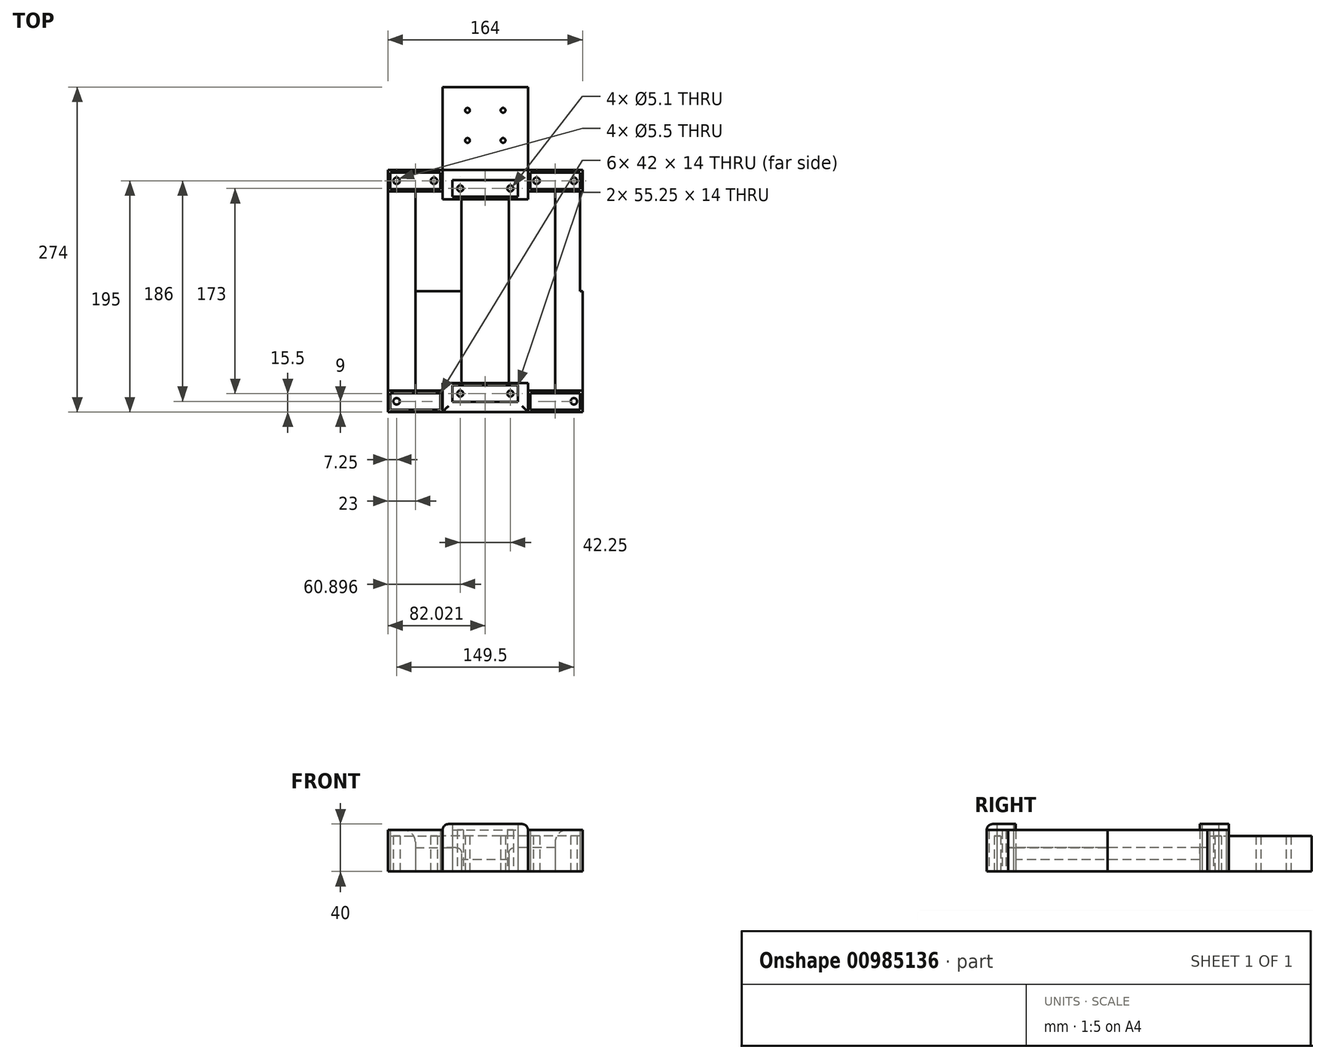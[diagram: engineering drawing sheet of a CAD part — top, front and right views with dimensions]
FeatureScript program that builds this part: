
annotation { "Feature Type Name" : "Feature", "Feature Type Description" : "" }
export const myFeature = defineFeature(function(context is Context, id is Id, definition is map)
    precondition{}
    {
        {
            var Q0;
            Q0=qCreatedBy(makeId("Top.planeOp"),FACE);
            var sketch = newSketch(context, id + "F0", { "sketchPlane" : qUnion([Q0])});
            skLineSegment(sketch, "E0.left", {"start": v(80, -100) * mm, "end": v(80, 100) * mm});
            skLineSegment(sketch, "E0.right", {"start": v(-80, -100) * mm, "end": v(-80, 100) * mm});
            skLineSegment(sketch, "E1.bottom", {"start": v(80, 100) * mm, "end": v(38, 100) * mm});
            skLineSegment(sketch, "E1.top", {"start": v(80, 86) * mm, "end": v(38, 86) * mm});
            skLineSegment(sketch, "E1.left", {"start": v(80, 100) * mm, "end": v(80, 86) * mm});
            skLineSegment(sketch, "E1.right", {"start": v(38, 100) * mm, "end": v(38, 86) * mm});
            skLineSegment(sketch, "E2.bottom", {"start": v(-80, 100) * mm, "end": v(-38, 100) * mm});
            skLineSegment(sketch, "E2.top", {"start": v(-80, 86) * mm, "end": v(-38, 86) * mm});
            skLineSegment(sketch, "E2.left", {"start": v(-80, 100) * mm, "end": v(-80, 86) * mm});
            skLineSegment(sketch, "E2.right", {"start": v(-38, 100) * mm, "end": v(-38, 86) * mm});
            skLineSegment(sketch, "E3.bottom", {"start": v(-27.6, 93.5) * mm, "end": v(27.65, 93.5) * mm});
            skLineSegment(sketch, "E3.top", {"start": v(-27.6, 79.5) * mm, "end": v(27.65, 79.5) * mm});
            skLineSegment(sketch, "E3.left", {"start": v(-27.6, 93.5) * mm, "end": v(-27.6, 79.5) * mm});
            skLineSegment(sketch, "E3.right", {"start": v(27.65, 93.5) * mm, "end": v(27.65, 79.5) * mm});
            skCircle(sketch, "E4", {"center": v(43.25, 93) * mm, "radius": 2.75 * mm});
            skPoint(sketch, "E4.centerSnap0", {"position": v(38, 93) * mm});
            skCircle(sketch, "E5", {"center": v(74.75, 93) * mm, "radius": 2.75 * mm});
            skCircle(sketch, "E6", {"center": v(-43.25, 93) * mm, "radius": 2.75 * mm});
            skPoint(sketch, "E6.centerSnap0", {"position": v(-38, 93) * mm});
            skCircle(sketch, "E7", {"center": v(-74.75, 93) * mm, "radius": 2.75 * mm});
            skPoint(sketch, "E7.centerSnap0", {"position": v(-80, 93) * mm});
            skCircle(sketch, "E8", {"center": v(-21.1, 86.5) * mm, "radius": 2.55 * mm});
            skPoint(sketch, "E8.centerSnap0", {"position": v(-27.6, 86.5) * mm});
            skCircle(sketch, "E9", {"center": v(21.15, 86.5) * mm, "radius": 2.55 * mm});
            skPoint(sketch, "E9.centerSnap0", {"position": v(27.65, 86.5) * mm});
            skLineSegment(sketch, "E10.2", {"start": v(-20, 77.5) * mm, "end": v(20, 77.5) * mm});
            skLineSegment(sketch, "E11.0", {"start": v(82, 102) * mm, "end": v(-82, 102) * mm});
            skLineSegment(sketch, "E11.1", {"start": v(82, -102) * mm, "end": v(82, 102) * mm});
            skLineSegment(sketch, "E11.3", {"start": v(-82, -102) * mm, "end": v(-82, 102) * mm});
            skLineSegment(sketch, "E12.0", {"start": v(-82, 84) * mm, "end": v(-36, 84) * mm});
            skLineSegment(sketch, "E12.1", {"start": v(-36, 102) * mm, "end": v(-36, 84) * mm});
            skLineSegment(sketch, "E13.0", {"start": v(82, 84) * mm, "end": v(36, 84) * mm});
            skLineSegment(sketch, "E13.1", {"start": v(36, 102) * mm, "end": v(36, 84) * mm});
            skLineSegment(sketch, "E14", {"start": v(-59, 84) * mm, "end": v(-59, -84) * mm});
            skLineSegment(sketch, "E15", {"start": v(59, 84) * mm, "end": v(59, -84) * mm});
            skLineSegment(sketch, "E16", {"start": v(82, 0) * mm, "end": v(80, 0) * mm});
            skLineSegment(sketch, "E17", {"start": v(80, 0) * mm, "end": v(59, 0) * mm});
            skLineSegment(sketch, "E18", {"start": v(59, 0) * mm, "end": v(0, 0) * mm});
            skLineSegment(sketch, "E19", {"start": v(0, 0) * mm, "end": v(-20, 0) * mm});
            skLineSegment(sketch, "E20", {"start": v(-59, 0) * mm, "end": v(-80, 0) * mm});
            skLineSegment(sketch, "E21.MirrorCS", {"start": v(-27.6, -93.5) * mm, "end": v(-27.6, -79.5) * mm});
            skCircle(sketch, "E22.MirrorC", {"center": v(-21.1, -86.5) * mm, "radius": 2.55 * mm});
            skCircle(sketch, "E23.MirrorC", {"center": v(74.75, -93) * mm, "radius": 2.75 * mm});
            skCircle(sketch, "E24.MirrorC", {"center": v(-74.75, -93) * mm, "radius": 2.75 * mm});
            skLineSegment(sketch, "E25.MirrorCS", {"start": v(-38, -100) * mm, "end": v(-38, -86) * mm});
            skLineSegment(sketch, "E26.MirrorCS", {"start": v(-36, -102) * mm, "end": v(-36, -84) * mm});
            skCircle(sketch, "E27.MirrorC", {"center": v(43.25, -93) * mm, "radius": 2.75 * mm});
            skCircle(sketch, "E28.MirrorC", {"center": v(21.15, -86.5) * mm, "radius": 2.55 * mm});
            skCircle(sketch, "E29.MirrorC", {"center": v(-43.25, -93) * mm, "radius": 2.75 * mm});
            skLineSegment(sketch, "E30.MirrorCS", {"start": v(27.65, -93.5) * mm, "end": v(27.65, -79.5) * mm});
            skLineSegment(sketch, "E31.MirrorCS", {"start": v(38, -100) * mm, "end": v(38, -86) * mm});
            skPoint(sketch, "E32.MirrorP", {"position": v(-38, -93) * mm});
            skLineSegment(sketch, "E33.MirrorCS", {"start": v(36, -102) * mm, "end": v(36, -84) * mm});
            skLineSegment(sketch, "E34.MirrorCS", {"start": v(80, -100) * mm, "end": v(80, -86) * mm});
            skPoint(sketch, "E35.MirrorP", {"position": v(-27.6, -86.5) * mm});
            skLineSegment(sketch, "E36.MirrorCS", {"start": v(-80, -100) * mm, "end": v(-80, -86) * mm});
            skLineSegment(sketch, "E37.MirrorCS", {"start": v(-82, -84) * mm, "end": v(-36, -84) * mm});
            skLineSegment(sketch, "E38.MirrorCS", {"start": v(-80, -86) * mm, "end": v(-38, -86) * mm});
            skPoint(sketch, "E39.MirrorP", {"position": v(38, -93) * mm});
            skLineSegment(sketch, "E40.MirrorCS", {"start": v(80, -86) * mm, "end": v(38, -86) * mm});
            skLineSegment(sketch, "E41.MirrorCS", {"start": v(-27.6, -79.5) * mm, "end": v(27.65, -79.5) * mm});
            skLineSegment(sketch, "E42.MirrorCS", {"start": v(82, -102) * mm, "end": v(-82, -102) * mm});
            skLineSegment(sketch, "E43.MirrorCS", {"start": v(82, -84) * mm, "end": v(36, -84) * mm});
            skPoint(sketch, "E44.MirrorP", {"position": v(27.65, -86.5) * mm});
            skLineSegment(sketch, "E45.MirrorCS", {"start": v(-27.6, -93.5) * mm, "end": v(27.65, -93.5) * mm});
            skLineSegment(sketch, "E46.MirrorCS", {"start": v(80, -100) * mm, "end": v(38, -100) * mm});
            skPoint(sketch, "E47.MirrorP", {"position": v(-80, -93) * mm});
            skLineSegment(sketch, "E48.MirrorCS", {"start": v(-80, -100) * mm, "end": v(-38, -100) * mm});
            skPoint(sketch, "E49", {"position": v(-80, 0) * mm});
            skPoint(sketch, "E50", {"position": v(-82, 0) * mm});
            skPoint(sketch, "E51", {"position": v(-80, 84) * mm});
            skPoint(sketch, "E52", {"position": v(-82, 84) * mm});
            skPoint(sketch, "E53", {"position": v(80, 84) * mm});
            skPoint(sketch, "E54", {"position": v(82, 84) * mm});
            skPoint(sketch, "E55", {"position": v(80, 0) * mm});
            skPoint(sketch, "E56", {"position": v(82, 0) * mm});
            skLineSegment(sketch, "E57", {"start": v(-82, 84) * mm, "end": v(-80, 84) * mm});
            skLineSegment(sketch, "E58", {"start": v(80, 84) * mm, "end": v(82, 84) * mm});
            skLineSegment(sketch, "E59", {"start": v(36, 102) * mm, "end": v(36, 100) * mm});
            skLineSegment(sketch, "E60", {"start": v(-82, 0) * mm, "end": v(-80, 0) * mm});
            skLineSegment(sketch, "E61", {"start": v(-82, -84) * mm, "end": v(-80, -84) * mm});
            skLineSegment(sketch, "E62", {"start": v(80, -84) * mm, "end": v(82, -84) * mm});
            skLineSegment(sketch, "E63", {"start": v(80, 0) * mm, "end": v(82, 0) * mm});
            skLineSegment(sketch, "E64", {"start": v(-38, 100) * mm, "end": v(-80, 100) * mm});
            skLineSegment(sketch, "E65", {"start": v(-59, -84) * mm, "end": v(-59, 0) * mm});
            skLineSegment(sketch, "E66", {"start": v(-59, 0) * mm, "end": v(-20, 0) * mm});
            skLineSegment(sketch, "E67", {"start": v(36, -102) * mm, "end": v(36, -77.5) * mm});
            skLineSegment(sketch, "E68", {"start": v(-36, -102) * mm, "end": v(-36, -77.5) * mm});
            skLineSegment(sketch, "E69", {"start": v(36, -77.5) * mm, "end": v(-36, -77.5) * mm});
            skLineSegment(sketch, "E70", {"start": v(20, -77.5) * mm, "end": v(20, 77.5) * mm});
            skLineSegment(sketch, "E71", {"start": v(-20, 77.5) * mm, "end": v(-20, -77.5) * mm});
            skLineSegment(sketch, "E72", {"start": v(36, 84) * mm, "end": v(36, 77.5) * mm});
            skLineSegment(sketch, "E73", {"start": v(36, 77.5) * mm, "end": v(20, 77.5) * mm});
            skLineSegment(sketch, "E74", {"start": v(-36, 84) * mm, "end": v(-36, 77.5) * mm});
            skLineSegment(sketch, "E75", {"start": v(-20, 77.5) * mm, "end": v(-36, 77.5) * mm});
            skLineSegment(sketch, "E76.bottom", {"start": v(-36, 102) * mm, "end": v(36, 102) * mm});
            skLineSegment(sketch, "E76.top", {"start": v(-36, 172) * mm, "end": v(36, 172) * mm});
            skLineSegment(sketch, "E76.left", {"start": v(-36, 102) * mm, "end": v(-36, 172) * mm});
            skLineSegment(sketch, "E76.right", {"start": v(36, 102) * mm, "end": v(36, 172) * mm});
            skLineSegment(sketch, "E77", {"start": v(0, 102) * mm, "end": v(0, 172) * mm});
            skCircle(sketch, "E78", {"center": v(-15, 127) * mm, "radius": 2 * mm});
            skCircle(sketch, "E79", {"center": v(-15, 152.4) * mm, "radius": 2 * mm});
            skCircle(sketch, "E80.MirrorC", {"center": v(15, 127) * mm, "radius": 2 * mm});
            skCircle(sketch, "E81.MirrorC", {"center": v(15, 152.4) * mm, "radius": 2 * mm});
            skSolve(sketch);
        }
        {
            var Q0;
            Q0=makeQuery(id+"F0.imprint","IMPRINT",FACE,{"disambiguationData":[TD([[makeQuery(id+"F0.imprint","IMPRINT",EDGE,{"derivedFrom":sQuery(id+"F0.wireOp",EDGE,"E2.bottom")}),-1.0]])]});
            var Q1;
            Q1=makeQuery(id+"F0.imprint","IMPRINT",FACE,{"disambiguationData":[TD([[makeQuery(id+"F0.imprint","IMPRINT",EDGE,{"derivedFrom":sQuery(id+"F0.wireOp",EDGE,"E1.bottom")}),1.0]])]});
            var Q2;
            Q2=makeQuery(id+"F0.imprint","IMPRINT",FACE,{"disambiguationData":[TD([[makeQuery(id+"F0.imprint","IMPRINT",EDGE,{"derivedFrom":sQuery(id+"F0.wireOp",EDGE,"ixyLcDFA-bc6J-Iatk-8igf-DqBppD76QXGP.bottom")}),1.0]])]});
            var Q3;
            Q3=makeQuery(id+"F0.imprint","IMPRINT",FACE,{"disambiguationData":[TD([[makeQuery(id+"F0.imprint","IMPRINT",EDGE,{"derivedFrom":sQuery(id+"F0.wireOp",EDGE,"OfFNVEAe-m7io-4Cfx-FPli-c9zqfDngx50L.bottom")}),-1.0]])]});
            var Q4;
            Q4=makeQuery(id+"F0.imprint","IMPRINT",FACE,{"disambiguationData":[TD([[makeQuery(id+"F0.imprint","IMPRINT",EDGE,{"derivedFrom":sQuery(id+"F0.wireOp",EDGE,"E24.MirrorC")}),1.0]])]});
            var Q5;
            Q5=makeQuery(id+"F0.imprint","IMPRINT",FACE,{"disambiguationData":[TD([[makeQuery(id+"F0.imprint","IMPRINT",EDGE,{"derivedFrom":sQuery(id+"F0.wireOp",EDGE,"E23.MirrorC")}),1.0]])]});
            var Q6;
            Q6=makeQuery(id+"F0.imprint","IMPRINT",FACE,{"disambiguationData":[TD([[makeQuery(id+"F0.imprint","IMPRINT",EDGE,{"derivedFrom":sQuery(id+"F0.wireOp",EDGE,"E1.top")}),-1.0]])]});
            var Q7;
            Q7=makeQuery(id+"F0.imprint","IMPRINT",FACE,{"disambiguationData":[TD([[makeQuery(id+"F0.imprint","IMPRINT",EDGE,{"derivedFrom":sQuery(id+"F0.wireOp",EDGE,"E2.top")}),1.0]])]});
            var Q8;
            Q8=makeQuery(id+"F0.imprint","IMPRINT",FACE,{"disambiguationData":[TD([[makeQuery(id+"F0.imprint","IMPRINT",EDGE,{"derivedFrom":sQuery(id+"F0.wireOp",EDGE,"E7")}),-1.0]])]});
            var Q9;
            Q9=makeQuery(id+"F0.imprint","IMPRINT",FACE,{"disambiguationData":[TD([[makeQuery(id+"F0.imprint","IMPRINT",EDGE,{"derivedFrom":sQuery(id+"F0.wireOp",EDGE,"E1.right")}),1.0]])]});
            extrude(context, id + "F1", {"entities" : qUnion([Q0, Q1, Q2, Q3, Q4, Q5, Q6, Q7, Q8, Q9]), "depth" : 30 * mm, "offsetDistance" : 25 * mm});
        }
        {
            var Q0;
            {var subQ1=sQuery(id+"F0.wireOp",EDGE,"E1.bottom");Q0=makeQuery(id+"F0.imprint","IMPRINT",FACE,{"disambiguationData":[TD([[makeQuery(id+"F0.imprint","IMPRINT",EDGE,{"derivedFrom":subQ1}),-1.0]])]});}
            var Q1;
            {var subQ0=sQuery(id+"F0.wireOp",EDGE,"E1.top");Q1=makeQuery(id+"F0.imprint","IMPRINT",FACE,{"disambiguationData":[TD([[makeQuery(id+"F0.imprint","IMPRINT",EDGE,{"derivedFrom":subQ0}),1.0]])]});}
            var Q2;
            {var subQ0=sQuery(id+"F0.wireOp",EDGE,"E2.bottom");Q2=makeQuery(id+"F0.imprint","IMPRINT",FACE,{"disambiguationData":[TD([[makeQuery(id+"F0.imprint","IMPRINT",EDGE,{"derivedFrom":subQ0}),1.0]])]});}
            var Q3;
            {var subQ4=sQuery(id+"F0.wireOp",EDGE,"E2.top");Q3=makeQuery(id+"F0.imprint","IMPRINT",FACE,{"disambiguationData":[TD([[makeQuery(id+"F0.imprint","IMPRINT",EDGE,{"derivedFrom":subQ4}),-1.0]])]});}
            var Q4;
            {var subQ1=sQuery(id+"F0.wireOp",EDGE,"ixyLcDFA-bc6J-Iatk-8igf-DqBppD76QXGP.top");Q4=makeQuery(id+"F0.imprint","IMPRINT",FACE,{"disambiguationData":[TD([[makeQuery(id+"F0.imprint","IMPRINT",EDGE,{"derivedFrom":subQ1}),1.0]])]});}
            var Q5;
            {var subQ4=sQuery(id+"F0.wireOp",EDGE,"ixyLcDFA-bc6J-Iatk-8igf-DqBppD76QXGP.bottom");Q5=makeQuery(id+"F0.imprint","IMPRINT",FACE,{"disambiguationData":[TD([[makeQuery(id+"F0.imprint","IMPRINT",EDGE,{"derivedFrom":subQ4}),-1.0]])]});}
            var Q6;
            {var subQ4=sQuery(id+"F0.wireOp",EDGE,"OfFNVEAe-m7io-4Cfx-FPli-c9zqfDngx50L.top");Q6=makeQuery(id+"F0.imprint","IMPRINT",FACE,{"disambiguationData":[TD([[makeQuery(id+"F0.imprint","IMPRINT",EDGE,{"derivedFrom":subQ4}),-1.0]])]});}
            var Q7;
            {var subQ1=sQuery(id+"F0.wireOp",EDGE,"OfFNVEAe-m7io-4Cfx-FPli-c9zqfDngx50L.bottom");Q7=makeQuery(id+"F0.imprint","IMPRINT",FACE,{"disambiguationData":[TD([[makeQuery(id+"F0.imprint","IMPRINT",EDGE,{"derivedFrom":subQ1}),1.0]])]});}
            var Q8;
            {var subQ9=sQuery(id+"F0.wireOp",EDGE,"E25.MirrorCS");Q8=makeQuery(id+"F0.imprint","IMPRINT",FACE,{"disambiguationData":[TD([[makeQuery(id+"F0.imprint","IMPRINT",EDGE,{"derivedFrom":subQ9}),-1.0]])]});}
            var Q9;
            {var subQ0=sQuery(id+"F0.wireOp",EDGE,"E36.MirrorCS");Q9=makeQuery(id+"F0.imprint","IMPRINT",FACE,{"disambiguationData":[TD([[makeQuery(id+"F0.imprint","IMPRINT",EDGE,{"derivedFrom":subQ0}),1.0]])]});}
            var Q10;
            {var subQ8=sQuery(id+"F0.wireOp",EDGE,"E31.MirrorCS");Q10=makeQuery(id+"F0.imprint","IMPRINT",FACE,{"disambiguationData":[TD([[makeQuery(id+"F0.imprint","IMPRINT",EDGE,{"derivedFrom":subQ8}),1.0]])]});}
            var Q11;
            {var subQ0=sQuery(id+"F0.wireOp",EDGE,"E34.MirrorCS");Q11=makeQuery(id+"F0.imprint","IMPRINT",FACE,{"disambiguationData":[TD([[makeQuery(id+"F0.imprint","IMPRINT",EDGE,{"derivedFrom":subQ0}),-1.0]])]});}
            var Q12;
            {var subQ0=sQuery(id+"F0.wireOp",EDGE,"E12.1");Q12=makeQuery(id+"F0.imprint","IMPRINT",FACE,{"disambiguationData":[TD([[makeQuery(id+"F0.imprint","IMPRINT",EDGE,{"derivedFrom":subQ0}),-1.0]])]});}
            var Q13;
            Q13=makeQuery(id+"F0.imprint","IMPRINT",FACE,{"disambiguationData":[TD([[makeQuery(id+"F0.imprint","IMPRINT",EDGE,{"derivedFrom":sQuery(id+"F0.wireOp",EDGE,"E1.right")}),-1.0]])]});
            extrude(context, id + "F2", {"entities" : qUnion([Q0, Q1, Q2, Q3, Q4, Q5, Q6, Q7, Q8, Q9, Q10, Q11, Q12, Q13]), "depth" : 35 * mm, "offsetDistance" : 25 * mm});
        }
        {
            var Q0;
            Q0=makeQuery(id+"F0.imprint","IMPRINT",FACE,{"disambiguationData":[TD([[makeQuery(id+"F0.imprint","IMPRINT",EDGE,{"derivedFrom":sQuery(id+"F0.wireOp",EDGE,"E3.bottom")}),-1.0]])]});
            var Q1;
            Q1=makeQuery(id+"F0.imprint","IMPRINT",FACE,{"disambiguationData":[TD([[makeQuery(id+"F0.imprint","IMPRINT",EDGE,{"derivedFrom":sQuery(id+"F0.wireOp",EDGE,"UbgPOWGu-DJYq-DXMP-9FCt-mUyMvT1JZ0WB.bottom")}),1.0]])]});
            var Q2;
            Q2=makeQuery(id+"F0.imprint","IMPRINT",FACE,{"disambiguationData":[TD([[makeQuery(id+"F0.imprint","IMPRINT",EDGE,{"derivedFrom":sQuery(id+"F0.wireOp",EDGE,"E21.MirrorCS")}),-1.0]])]});
            var Q3;
            Q3=makeQuery(id+"F0.imprint","IMPRINT",FACE,{"disambiguationData":[TD([[makeQuery(id+"F0.imprint","IMPRINT",EDGE,{"derivedFrom":sQuery(id+"F0.wireOp",EDGE,"E8")}),-1.0]])]});
            extrude(context, id + "F3", {"entities" : qUnion([Q0, Q1, Q2, Q3]), "depth" : 35 * mm, "offsetDistance" : 25 * mm});
        }
        {
            var Q0;
            Q0=makeQuery(id+"F0.imprint","IMPRINT",FACE,{"disambiguationData":[TD([[makeQuery(id+"F0.imprint","IMPRINT",EDGE,{"derivedFrom":sQuery(id+"F0.wireOp",EDGE,"UbgPOWGu-DJYq-DXMP-9FCt-mUyMvT1JZ0WB.top")}),1.0]])]});
            var Q1;
            {var subQ0=sQuery(id+"F0.wireOp",EDGE,"UbgPOWGu-DJYq-DXMP-9FCt-mUyMvT1JZ0WB.bottom");Q1=makeQuery(id+"F0.imprint","IMPRINT",FACE,{"disambiguationData":[TD([[makeQuery(id+"F0.imprint","IMPRINT",EDGE,{"derivedFrom":subQ0}),-1.0]])]});}
            var Q2;
            Q2=makeQuery(id+"F0.imprint","IMPRINT",FACE,{"disambiguationData":[TD([[makeQuery(id+"F0.imprint","IMPRINT",EDGE,{"derivedFrom":sQuery(id+"F0.wireOp",EDGE,"E3.bottom")}),1.0]])]});
            var Q3;
            Q3=makeQuery(id+"F0.imprint","IMPRINT",FACE,{"disambiguationData":[TD([[makeQuery(id+"F0.imprint","IMPRINT",EDGE,{"derivedFrom":sQuery(id+"F0.wireOp",EDGE,"E21.MirrorCS")}),1.0]])]});
            var Q4;
            {var subQ10=sQuery(id+"F0.wireOp",EDGE,"qVaEij7k-nwjH-SPuv-bkV3-loI1qYVZHqOl");Q4=makeQuery(id+"F0.imprint","IMPRINT",FACE,{"disambiguationData":[TD([[makeQuery(id+"F0.imprint","IMPRINT",EDGE,{"derivedFrom":subQ10}),1.0]])]});}
            var Q5;
            {var subQ2=sQuery(id+"F0.wireOp",EDGE,"E12.1");Q5=makeQuery(id+"F0.imprint","IMPRINT",FACE,{"disambiguationData":[TD([[makeQuery(id+"F0.imprint","IMPRINT",EDGE,{"derivedFrom":subQ2}),1.0]])]});}
            extrude(context, id + "F4", {"entities" : qUnion([Q0, Q1, Q2, Q3, Q4, Q5]), "depth" : 40 * mm, "offsetDistance" : 25 * mm});
        }
        {
            var Q0;
            {var subQ0=sQuery(id+"F0.wireOp",EDGE,"B5Z4tnl7-zgow-OxXi-EMlq-tNImqLLrCm8m");Q0=makeQuery(id+"F0.imprint","IMPRINT",FACE,{"disambiguationData":[TD([[makeQuery(id+"F0.imprint","IMPRINT",EDGE,{"derivedFrom":subQ0}),-1.0]])]});}
            var Q1;
            {var subQ0=sQuery(id+"F0.wireOp",EDGE,"QeB9K7Id-tPgK-ENxB-AcUf-C9a2ECh6eyOd");Q1=makeQuery(id+"F0.imprint","IMPRINT",FACE,{"disambiguationData":[TD([[makeQuery(id+"F0.imprint","IMPRINT",EDGE,{"derivedFrom":subQ0}),1.0]])]});}
            var Q2;
            {var subQ3=sQuery(id+"F0.wireOp",EDGE,"b8552f40-8e1e-479f-b918-41427cde39ce1.MirrorCS");Q2=makeQuery(id+"F0.imprint","IMPRINT",FACE,{"disambiguationData":[TD([[makeQuery(id+"F0.imprint","IMPRINT",EDGE,{"derivedFrom":subQ3}),1.0]])]});}
            var Q3;
            {var subQ0=sQuery(id+"F0.wireOp",EDGE,"b8552f40-8e1e-479f-b918-41427cde39ce12.MirrorCS");var subQ1=sQuery(id+"F0.wireOp",EDGE,"tyTy7cMs-IovG-FTIG-svWU-RZ1L8kjrpybv");var subQ2=makeQuery(id+"F0.imprint","INTERSECT",VERTEX,{"derivedFrom":[subQ1,subQ0]});Q3=makeQuery(id+"F0.imprint","IMPRINT",FACE,{"disambiguationData":[TD([[makeQuery(id+"F0.imprint","IMPRINT",EDGE,{"disambiguationData":[TD([[subQ2,1.0]])],"derivedFrom":subQ1}),1.0]])]});}
            var Q4;
            {var subQ5=sQuery(id+"F0.wireOp",EDGE,"OglT18Nm-HUVC-Pnps-TW8b-jYMKbPkvL7uU");Q4=makeQuery(id+"F0.imprint","IMPRINT",FACE,{"disambiguationData":[TD([[makeQuery(id+"F0.imprint","IMPRINT",EDGE,{"derivedFrom":subQ5}),-1.0]])]});}
            var Q5;
            {var subQ3=sQuery(id+"F0.wireOp",EDGE,"C9wmSgbj-CDq8-hHrZ-SwvS-kieF0k5TPAWY");Q5=makeQuery(id+"F0.imprint","IMPRINT",FACE,{"disambiguationData":[TD([[makeQuery(id+"F0.imprint","IMPRINT",EDGE,{"derivedFrom":subQ3}),1.0]])]});}
            var Q6;
            {var subQ1=sQuery(id+"F0.wireOp",EDGE,"E14");Q6=makeQuery(id+"F0.imprint","IMPRINT",FACE,{"disambiguationData":[TD([[makeQuery(id+"F0.imprint","IMPRINT",EDGE,{"derivedFrom":subQ1}),1.0]])]});}
            var Q7;
            {var subQ6=sQuery(id+"F0.wireOp",EDGE,"E65");Q7=makeQuery(id+"F0.imprint","IMPRINT",FACE,{"disambiguationData":[TD([[makeQuery(id+"F0.imprint","IMPRINT",EDGE,{"derivedFrom":subQ6}),-1.0]])]});}
            var Q8;
            {var subQ0=sQuery(id+"F0.wireOp",EDGE,"E43.MirrorCS");var subQ1=sQuery(id+"F0.wireOp",EDGE,"E15");var subQ2=makeQuery(id+"F0.imprint","INTERSECT",VERTEX,{"derivedFrom":[subQ1,subQ0]});Q8=makeQuery(id+"F0.imprint","IMPRINT",FACE,{"disambiguationData":[TD([[makeQuery(id+"F0.imprint","IMPRINT",EDGE,{"disambiguationData":[TD([[subQ2,-1.0]])],"derivedFrom":subQ0}),-1.0]])]});}
            var Q9;
            {var subQ3=sQuery(id+"F0.wireOp",EDGE,"E72");Q9=makeQuery(id+"F0.imprint","IMPRINT",FACE,{"disambiguationData":[TD([[makeQuery(id+"F0.imprint","IMPRINT",EDGE,{"derivedFrom":subQ3}),1.0]])]});}
            extrude(context, id + "F5", {"entities" : qUnion([Q0, Q1, Q2, Q3, Q4, Q5, Q6, Q7, Q8, Q9]), "depth" : 20 * mm, "offsetDistance" : 25 * mm});
        }
        {
            var Q0;
            Q0=makeQuery(id+"F0.imprint","IMPRINT",FACE,{"disambiguationData":[TD([[makeQuery(id+"F0.imprint","IMPRINT",EDGE,{"derivedFrom":sQuery(id+"F0.wireOp",EDGE,"E10.2")}),-1.0]])]});
            var Q1;
            {var subQ0=sQuery(id+"F0.wireOp",EDGE,"E19");Q1=makeQuery(id+"F0.imprint","IMPRINT",FACE,{"disambiguationData":[TD([[makeQuery(id+"F0.imprint","IMPRINT",EDGE,{"derivedFrom":subQ0}),1.0]])]});}
            var Q2;
            Q2=makeQuery(id+"F0.imprint","IMPRINT",FACE,{"disambiguationData":[TD([[makeQuery(id+"F0.imprint","IMPRINT",EDGE,{"derivedFrom":sQuery(id+"F0.wireOp",EDGE,"P8kr6sO9-KCci-oqqV-lbCG-12AdMWymWlzo")}),-1.0]])]});
            var Q3;
            {var subQ1=sQuery(id+"F0.wireOp",EDGE,"E19");Q3=makeQuery(id+"F0.imprint","IMPRINT",FACE,{"disambiguationData":[TD([[makeQuery(id+"F0.imprint","IMPRINT",EDGE,{"derivedFrom":subQ1}),-1.0]])]});}
            extrude(context, id + "F6", {"entities" : qUnion([Q0, Q1, Q2, Q3]), "depth" : 10 * mm, "offsetDistance" : 25 * mm});
        }
        {
            var Q0;
            {var subQ1=sQuery(id+"F0.wireOp",EDGE,"E2.bottom");Q0=makeQuery(id+"F0.imprint","IMPRINT",FACE,{"disambiguationData":[TD([[makeQuery(id+"F0.imprint","IMPRINT",EDGE,{"derivedFrom":subQ1}),1.0]])]});}
            var Q1;
            {var subQ0=sQuery(id+"F0.wireOp",EDGE,"E1.bottom");Q1=makeQuery(id+"F0.imprint","IMPRINT",FACE,{"disambiguationData":[TD([[makeQuery(id+"F0.imprint","IMPRINT",EDGE,{"derivedFrom":subQ0}),-1.0]])]});}
            var Q2;
            {var subQ0=sQuery(id+"F0.wireOp",EDGE,"b3zk2VQc-cE7L-r2go-jK9M-t36oJfSmH84w");var subQ1=sQuery(id+"F0.wireOp",EDGE,"E0.left");var subQ2=makeQuery(id+"F0.imprint","INTERSECT",VERTEX,{"derivedFrom":[subQ1,subQ0]});Q2=makeQuery(id+"F0.imprint","IMPRINT",FACE,{"disambiguationData":[TD([[makeQuery(id+"F0.imprint","IMPRINT",EDGE,{"disambiguationData":[TD([[subQ2,-1.0]])],"derivedFrom":subQ1}),-1.0]])]});}
            var Q3;
            {var subQ0=sQuery(id+"F0.wireOp",EDGE,"E36.MirrorCS");Q3=makeQuery(id+"F0.imprint","IMPRINT",FACE,{"disambiguationData":[TD([[makeQuery(id+"F0.imprint","IMPRINT",EDGE,{"derivedFrom":subQ0}),1.0]])]});}
            var Q4;
            {var subQ0=sQuery(id+"F0.wireOp",EDGE,"E16");Q4=makeQuery(id+"F0.imprint","IMPRINT",FACE,{"disambiguationData":[TD([[makeQuery(id+"F0.imprint","IMPRINT",EDGE,{"derivedFrom":subQ0}),1.0]])]});}
            var Q5;
            {var subQ0=sQuery(id+"F0.wireOp",EDGE,"E34.MirrorCS");Q5=makeQuery(id+"F0.imprint","IMPRINT",FACE,{"disambiguationData":[TD([[makeQuery(id+"F0.imprint","IMPRINT",EDGE,{"derivedFrom":subQ0}),-1.0]])]});}
            var Q6;
            {var subQ0=sQuery(id+"F0.wireOp",EDGE,"E17");Q6=makeQuery(id+"F0.imprint","IMPRINT",FACE,{"disambiguationData":[TD([[makeQuery(id+"F0.imprint","IMPRINT",EDGE,{"derivedFrom":subQ0}),1.0]])]});}
            var Q7;
            {var subQ0=sQuery(id+"F0.wireOp",EDGE,"E37.MirrorCS");var subQ1=sQuery(id+"F0.wireOp",EDGE,"E0.right");var subQ2=makeQuery(id+"F0.imprint","INTERSECT",VERTEX,{"derivedFrom":[subQ1,subQ0]});Q7=makeQuery(id+"F0.imprint","IMPRINT",FACE,{"disambiguationData":[TD([[makeQuery(id+"F0.imprint","IMPRINT",EDGE,{"disambiguationData":[TD([[subQ2,-1.0]])],"derivedFrom":subQ1}),-1.0]])]});}
            var Q8;
            {var subQ0=sQuery(id+"F0.wireOp",EDGE,"b3zk2VQc-cE7L-r2go-jK9M-t36oJfSmH84w");var subQ1=sQuery(id+"F0.wireOp",EDGE,"E0.left");var subQ2=makeQuery(id+"F0.imprint","INTERSECT",VERTEX,{"derivedFrom":[subQ1,subQ0]});Q8=makeQuery(id+"F0.imprint","IMPRINT",FACE,{"disambiguationData":[TD([[makeQuery(id+"F0.imprint","IMPRINT",EDGE,{"disambiguationData":[TD([[subQ2,-1.0]])],"derivedFrom":subQ1}),1.0]])]});}
            var Q9;
            {var subQ0=sQuery(id+"F0.wireOp",EDGE,"E20");Q9=makeQuery(id+"F0.imprint","IMPRINT",FACE,{"disambiguationData":[TD([[makeQuery(id+"F0.imprint","IMPRINT",EDGE,{"derivedFrom":subQ0}),-1.0]])]});}
            var Q10;
            {var subQ3=sQuery(id+"F0.wireOp",EDGE,"E57");Q10=makeQuery(id+"F0.imprint","IMPRINT",FACE,{"disambiguationData":[TD([[makeQuery(id+"F0.imprint","IMPRINT",EDGE,{"derivedFrom":subQ3}),-1.0]])]});}
            var Q11;
            {var subQ0=sQuery(id+"F0.wireOp",EDGE,"E37.MirrorCS");var subQ1=sQuery(id+"F0.wireOp",EDGE,"E0.right");var subQ2=makeQuery(id+"F0.imprint","INTERSECT",VERTEX,{"derivedFrom":[subQ1,subQ0]});Q11=makeQuery(id+"F0.imprint","IMPRINT",FACE,{"disambiguationData":[TD([[makeQuery(id+"F0.imprint","IMPRINT",EDGE,{"disambiguationData":[TD([[subQ2,-1.0]])],"derivedFrom":subQ1}),1.0]])]});}
            var Q12;
            {var subQ0=sQuery(id+"F0.wireOp",EDGE,"E57");Q12=makeQuery(id+"F0.imprint","IMPRINT",FACE,{"disambiguationData":[TD([[makeQuery(id+"F0.imprint","IMPRINT",EDGE,{"derivedFrom":subQ0}),-1.0]])]});}
            var Q13;
            {var subQ2=sQuery(id+"F0.wireOp",EDGE,"E62");Q13=makeQuery(id+"F0.imprint","IMPRINT",FACE,{"disambiguationData":[TD([[makeQuery(id+"F0.imprint","IMPRINT",EDGE,{"derivedFrom":subQ2}),1.0]])]});}
            var Q14;
            {var subQ0=sQuery(id+"F0.wireOp",EDGE,"E17");Q14=makeQuery(id+"F0.imprint","IMPRINT",FACE,{"disambiguationData":[TD([[makeQuery(id+"F0.imprint","IMPRINT",EDGE,{"derivedFrom":subQ0}),-1.0]])]});}
            var Q15;
            {var subQ0=sQuery(id+"F0.wireOp",EDGE,"E63");Q15=makeQuery(id+"F0.imprint","IMPRINT",FACE,{"disambiguationData":[TD([[makeQuery(id+"F0.imprint","IMPRINT",EDGE,{"derivedFrom":subQ0}),1.0]])]});}
            var Q16;
            {var subQ0=sQuery(id+"F0.wireOp",EDGE,"E60");Q16=makeQuery(id+"F0.imprint","IMPRINT",FACE,{"disambiguationData":[TD([[makeQuery(id+"F0.imprint","IMPRINT",EDGE,{"derivedFrom":subQ0}),1.0]])]});}
            extrude(context, id + "F7", {"entities" : qUnion([Q0, Q1, Q2, Q3, Q4, Q5, Q6, Q7, Q8, Q9, Q10, Q11, Q12, Q13, Q14, Q15, Q16]), "depth" : 35 * mm, "offsetDistance" : 25 * mm});
        }
        {
            var Q0;
            Q0=makeQuery(id+"F7.opExtrude","CAP_EDGE",EDGE,{"disambiguationData":[OSD([sQuery(id+"F0.wireOp",EDGE,"E15")])],"isStart":false});
            var Q1;
            Q1=makeQuery(id+"F7.opExtrude","CAP_EDGE",EDGE,{"disambiguationData":[OSD([sQuery(id+"F0.wireOp",EDGE,"E14"),sQuery(id+"F0.wireOp",EDGE,"E65")])],"isStart":false});
            fillet(context, id + "F8", {"entities" : qUnion([Q0, Q1]), "radius" : 10 * mm, "tangentPropagation" : true, "allowEdgeOverflow" : false});
        }
        {
            var Q0;
            Q0=makeQuery(id+"F4.opExtrude","CAP_EDGE",EDGE,{"disambiguationData":[OSD([sQuery(id+"F0.wireOp",EDGE,"E11.0")])],"isStart":false});
            var Q1;
            Q1=makeQuery(id+"F4.opExtrude","CAP_EDGE",EDGE,{"disambiguationData":[OSD([sQuery(id+"F0.wireOp",EDGE,"E12.1"),sQuery(id+"F0.wireOp",EDGE,"E74")])],"isStart":false});
            var Q2;
            Q2=makeQuery(id+"F4.opExtrude","CAP_EDGE",EDGE,{"disambiguationData":[OSD([sQuery(id+"F0.wireOp",EDGE,"E13.1"),sQuery(id+"F0.wireOp",EDGE,"E72")])],"isStart":false});
            var Q3;
            Q3=makeQuery(id+"F4.opExtrude","CAP_EDGE",EDGE,{"disambiguationData":[OSD([sQuery(id+"F0.wireOp",EDGE,"E67")])],"isStart":false});
            var Q4;
            Q4=makeQuery(id+"F4.opExtrude","CAP_EDGE",EDGE,{"disambiguationData":[OSD([sQuery(id+"F0.wireOp",EDGE,"E42.MirrorCS")])],"isStart":false});
            var Q5;
            Q5=makeQuery(id+"F4.opExtrude","CAP_EDGE",EDGE,{"disambiguationData":[OSD([sQuery(id+"F0.wireOp",EDGE,"E68")])],"isStart":false});
            fillet(context, id + "F9", {"entities" : qUnion([Q0, Q1, Q2, Q3, Q4, Q5]), "radius" : 5 * mm, "tangentPropagation" : true, "allowEdgeOverflow" : false});
        }
        {
            var Q0;
            Q0=makeQuery(id+"F5.opExtrude","CAP_EDGE",EDGE,{"disambiguationData":[OSD([sQuery(id+"F0.wireOp",EDGE,"E71")])],"isStart":false});
            var Q1;
            Q1=makeQuery(id+"F5.opExtrude","CAP_EDGE",EDGE,{"disambiguationData":[OSD([sQuery(id+"F0.wireOp",EDGE,"E70")])],"isStart":false});
            fillet(context, id + "F10", {"entities" : qUnion([Q0, Q1]), "radius" : 5 * mm, "tangentPropagation" : true, "rho" : .5, "crossSection" : FilletCrossSection.CONIC, "allowEdgeOverflow" : false});
        }
        {
            var Q0;
            {var subQ1=sQuery(id+"F0.wireOp",EDGE,"E76.left");Q0=makeQuery(id+"F0.imprint","IMPRINT",FACE,{"disambiguationData":[TD([[makeQuery(id+"F0.imprint","IMPRINT",EDGE,{"derivedFrom":subQ1}),-1.0]])]});}
            var Q1;
            {var subQ0=sQuery(id+"F0.wireOp",EDGE,"E76.right");Q1=makeQuery(id+"F0.imprint","IMPRINT",FACE,{"disambiguationData":[TD([[makeQuery(id+"F0.imprint","IMPRINT",EDGE,{"derivedFrom":subQ0}),1.0]])]});}
            extrude(context, id + "F11", {"entities" : qUnion([Q0, Q1]), "depth" : 30 * mm, "offsetDistance" : 25 * mm});
        }
    });
